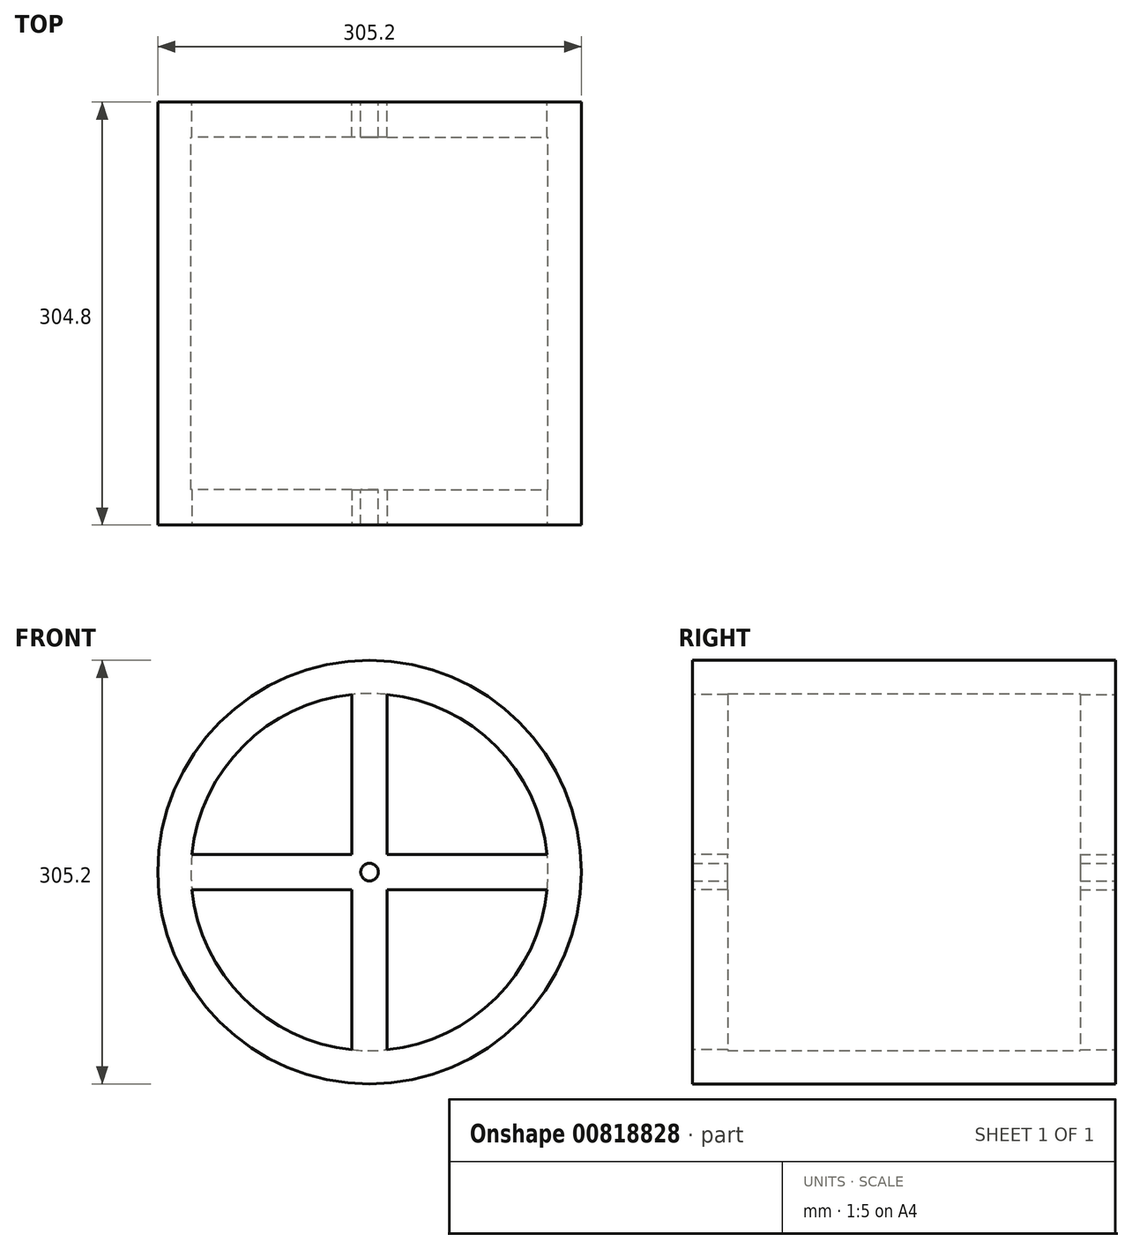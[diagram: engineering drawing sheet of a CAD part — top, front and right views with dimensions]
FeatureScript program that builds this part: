
annotation { "Feature Type Name" : "Feature", "Feature Type Description" : "" }
export const myFeature = defineFeature(function(context is Context, id is Id, definition is map)
    precondition{}
    {
        {
            var Q0;
            Q0=qCreatedBy(makeId("Front.planeOp"),FACE);
            var sketch = newSketch(context, id + "F0", { "sketchPlane" : qUnion([Q0])});
            skCircle(sketch, "E0", {"center": v(0, 0) * mm, "radius": 152.6 * mm});
            skCircle(sketch, "E1", {"center": v(0, 0) * mm, "radius": 128.6 * mm});
            skSolve(sketch);
        }
        {
            var Q0;
            Q0=makeQuery(id+"F0.imprint","IMPRINT",FACE,{"disambiguationData":[TD([[makeQuery(id+"F0.imprint","IMPRINT",EDGE,{"derivedFrom":sQuery(id+"F0.wireOp",EDGE,"E0")}),1.0]])]});
            extrude(context, id + "F1", {"entities" : qUnion([Q0]), "depth" : 304.8 * mm, "offsetDistance" : 25 * mm});
        }
        {
            var Q0;
            Q0=makeQuery(id+"F1.opExtrude","CAP_FACE",FACE,{"disambiguationData":[OSD([sQuery(id+"F0.wireOp",EDGE,"E0"),sQuery(id+"F0.wireOp",EDGE,"E1")])],"isStart":false});
            var sketch = newSketch(context, id + "F2", { "sketchPlane" : qUnion([Q0])});
            skLineSegment(sketch, "E2", {"start": v(0, 128.6) * mm, "end": v(0, -128.6) * mm, "construction": true});
            skLineSegment(sketch, "E3", {"start": v(-12.7, 127.97) * mm, "end": v(-12.7, -127.97) * mm});
            skLineSegment(sketch, "E4.MirrorCS", {"start": v(12.7, 127.97) * mm, "end": v(12.7, -127.97) * mm});
            skLineSegment(sketch, "E5", {"start": v(0, 0) * mm, "end": v(128.6, 0) * mm, "construction": true});
            skPoint(sketch, "E5.endSnap0", {"position": v(12.7, 0) * mm});
            skLineSegment(sketch, "E6", {"start": v(0, 0) * mm, "end": v(-128.6, 0) * mm, "construction": true});
            skLineSegment(sketch, "E7", {"start": v(12.7, -12.7) * mm, "end": v(127.97, -12.7) * mm});
            skLineSegment(sketch, "E8.MirrorCS", {"start": v(12.7, 12.7) * mm, "end": v(127.97, 12.7) * mm});
            skLineSegment(sketch, "E9.MirrorCS", {"start": v(-12.7, 12.7) * mm, "end": v(-127.97, 12.7) * mm});
            skLineSegment(sketch, "E10.MirrorCS", {"start": v(-12.7, -12.7) * mm, "end": v(-127.97, -12.7) * mm});
            skArc(sketch, "E11.0", {"start": v(-127.97, 12.7) * mm, "mid": v(-128.6, 0) * mm, "end": v(-127.97, -12.7) * mm});
            skArc(sketch, "E12.trimOffspring", {"start": v(12.7, 127.97) * mm, "mid": v(0, 128.6) * mm, "end": v(-12.7, 127.97) * mm});
            skArc(sketch, "E13.trimOffspring", {"start": v(127.97, -12.7) * mm, "mid": v(128.6, 0) * mm, "end": v(127.97, 12.7) * mm});
            skArc(sketch, "E14.trimOffspring", {"start": v(-12.7, -127.97) * mm, "mid": v(0, -128.6) * mm, "end": v(12.7, -127.97) * mm});
            skSolve(sketch);
        }
        {
            var Q0;
            Q0 = qSketchRegion(id + "F2", true);
            var Q1;
            {var subQ0=sQuery(id+"F2.wireOp",EDGE,"E9.MirrorCS");Q1=makeQuery(id+"F2.imprint","IMPRINT",FACE,{"disambiguationData":[TD([[makeQuery(id+"F2.imprint","IMPRINT",EDGE,{"derivedFrom":subQ0}),1.0]])]});}
            var Q2;
            {var subQ0=sQuery(id+"F2.wireOp",EDGE,"E7");Q2=makeQuery(id+"F2.imprint","IMPRINT",FACE,{"disambiguationData":[TD([[makeQuery(id+"F2.imprint","IMPRINT",EDGE,{"derivedFrom":subQ0}),1.0]])]});}
            var Q3;
            {var subQ1=makeQuery(id+"F1.opExtrude","CAP_EDGE",EDGE,{"disambiguationData":[OSD([sQuery(id+"F0.wireOp",EDGE,"E1")])],"isStart":false});var subQ4=sQuery(id+"F2.wireOp",EDGE,"E3");var subQ9=makeQuery(id+"F2.imprint","INTERSECT",VERTEX,{"disambiguationData":[OD(0.0)],"derivedFrom":[subQ1,subQ4]});Q3=makeQuery(id+"F2.imprint","IMPRINT",FACE,{"disambiguationData":[TD([[makeQuery(id+"F2.imprint","IMPRINT",EDGE,{"disambiguationData":[TD([[subQ9,-1.0]])],"derivedFrom":subQ4}),1.0]])]});}
            extrude(context, id + "F3", {"entities" : qUnion([Q0, Q1, Q2, Q3]), "operationType" : NewBodyOperationType.ADD, "oppositeDirection" : true, "depth" : 25.4 * mm, "offsetDistance" : 25 * mm});
        }
        {
            var Q0;
            Q0=makeQuery(id+"F1.opExtrude","CAP_FACE",FACE,{"disambiguationData":[OSD([sQuery(id+"F0.wireOp",EDGE,"E0"),sQuery(id+"F0.wireOp",EDGE,"E1")])],"isStart":true});
            var sketch = newSketch(context, id + "F4", { "sketchPlane" : qUnion([Q0])});
            skLineSegment(sketch, "E15.0", {"start": v(-12.7, 12.7) * mm, "end": v(-127.97, 12.7) * mm});
            skLineSegment(sketch, "E15.1", {"start": v(-12.7, 127.97) * mm, "end": v(-12.7, 12.7) * mm});
            skLineSegment(sketch, "E15.2", {"start": v(12.7, 127.97) * mm, "end": v(12.7, 12.7) * mm});
            skLineSegment(sketch, "E15.3", {"start": v(12.7, 12.7) * mm, "end": v(127.97, 12.7) * mm});
            skLineSegment(sketch, "E15.4", {"start": v(12.7, -12.7) * mm, "end": v(127.97, -12.7) * mm});
            skLineSegment(sketch, "E15.5", {"start": v(12.7, -12.7) * mm, "end": v(12.7, -127.97) * mm});
            skLineSegment(sketch, "E15.6", {"start": v(-12.7, -12.7) * mm, "end": v(-12.7, -127.97) * mm});
            skLineSegment(sketch, "E15.7", {"start": v(-12.7, -12.7) * mm, "end": v(-127.97, -12.7) * mm});
            skArc(sketch, "E16.0", {"start": v(-127.97, 12.7) * mm, "mid": v(-128.6, 0) * mm, "end": v(-127.97, -12.7) * mm});
            skArc(sketch, "E17.trimOffspring", {"start": v(12.7, 127.97) * mm, "mid": v(0, 128.6) * mm, "end": v(-12.7, 127.97) * mm});
            skArc(sketch, "E18.trimOffspring", {"start": v(127.97, -12.7) * mm, "mid": v(128.6, 0) * mm, "end": v(127.97, 12.7) * mm});
            skArc(sketch, "E19.trimOffspring", {"start": v(-12.7, -127.97) * mm, "mid": v(0, -128.6) * mm, "end": v(12.7, -127.97) * mm});
            skSolve(sketch);
        }
        {
            var Q0;
            Q0=makeQuery(id+"F4.imprint","IMPRINT",FACE,{"disambiguationData":[TD([[makeQuery(id+"F4.imprint","IMPRINT",EDGE,{"derivedFrom":sQuery(id+"F4.wireOp",EDGE,"E15.0")}),1.0]])]});
            extrude(context, id + "F5", {"entities" : qUnion([Q0]), "operationType" : NewBodyOperationType.ADD, "oppositeDirection" : true, "depth" : 25.4 * mm, "offsetDistance" : 25 * mm});
        }
        {
            var Q0;
            Q0=makeQuery(id+"F5.boolean.opBoolean","MERGE",FACE,{"derivedFrom":[makeQuery(id+"F1.opExtrude","CAP_FACE",FACE,{"disambiguationData":[OSD([sQuery(id+"F0.wireOp",EDGE,"E0"),sQuery(id+"F0.wireOp",EDGE,"E1")])],"isStart":true}),makeQuery(id+"F5.opExtrude","CAP_FACE",FACE,{"disambiguationData":[OSD([sQuery(id+"F4.wireOp",EDGE,"E15.0"),sQuery(id+"F4.wireOp",EDGE,"E15.1"),sQuery(id+"F4.wireOp",EDGE,"E15.2"),sQuery(id+"F4.wireOp",EDGE,"E15.3"),sQuery(id+"F4.wireOp",EDGE,"E15.4"),sQuery(id+"F4.wireOp",EDGE,"E15.5"),sQuery(id+"F4.wireOp",EDGE,"E15.6"),sQuery(id+"F4.wireOp",EDGE,"E15.7"),sQuery(id+"F4.wireOp",EDGE,"E16.0"),sQuery(id+"F4.wireOp",EDGE,"E17.trimOffspring"),sQuery(id+"F4.wireOp",EDGE,"E18.trimOffspring"),sQuery(id+"F4.wireOp",EDGE,"E19.trimOffspring")])],"isStart":true})]});
            var sketch = newSketch(context, id + "F6", { "sketchPlane" : qUnion([Q0])});
            skCircle(sketch, "E20", {"center": v(0, 0) * mm, "radius": 6.35 * mm});
            skSolve(sketch);
        }
        {
            var Q0;
            Q0=makeQuery(id+"F6.imprint","IMPRINT",FACE,{"disambiguationData":[TD([[makeQuery(id+"F6.imprint","IMPRINT",EDGE,{"derivedFrom":sQuery(id+"F6.wireOp",EDGE,"E20")}),1.0]])]});
            extrude(context, id + "F7", {"entities" : qUnion([Q0]), "operationType" : NewBodyOperationType.REMOVE, "oppositeDirection" : true, "depth" : 382 * mm, "offsetDistance" : 25 * mm});
        }
    });
